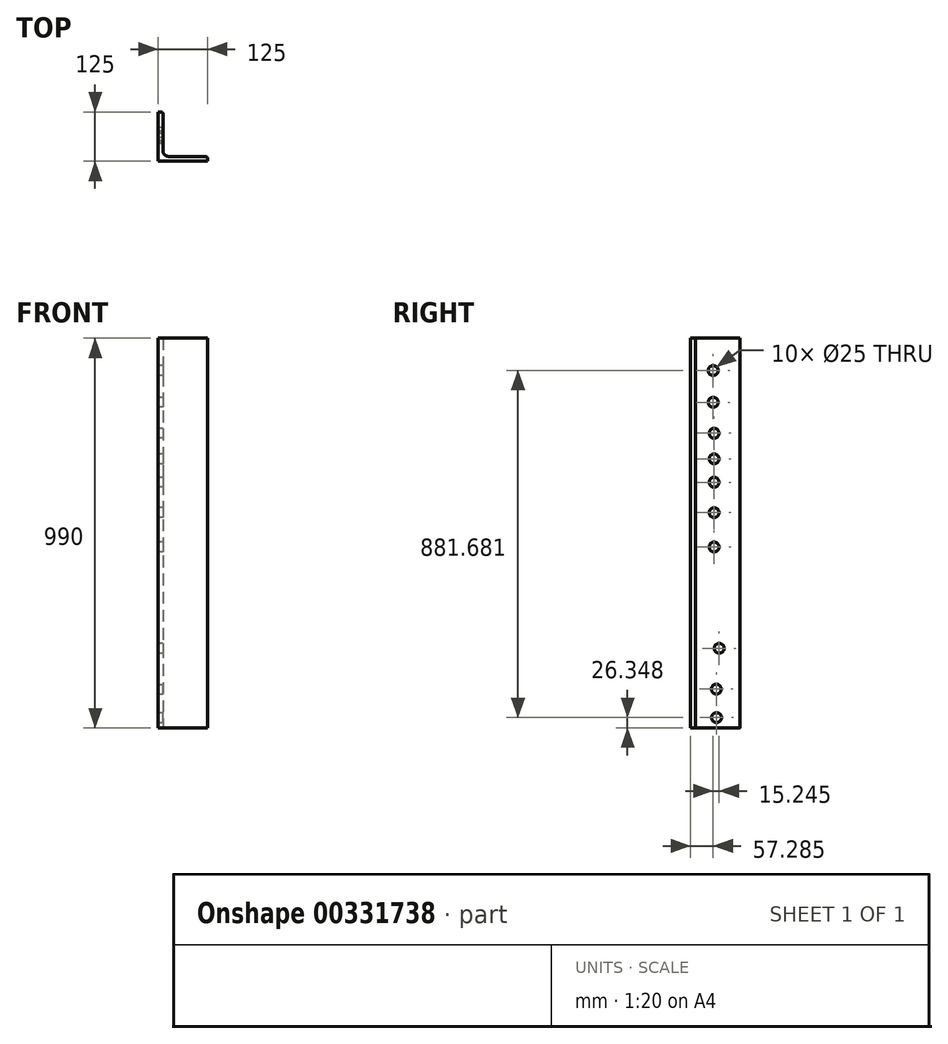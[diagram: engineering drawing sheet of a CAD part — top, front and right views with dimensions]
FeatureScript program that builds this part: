
annotation { "Feature Type Name" : "Feature", "Feature Type Description" : "" }
export const myFeature = defineFeature(function(context is Context, id is Id, definition is map)
    precondition{}
    {
        {
            var Q0;
            Q0=qCreatedBy(makeId("Top.planeOp"),FACE);
            var sketch = newSketch(context, id + "F0", { "sketchPlane" : qUnion([Q0])});
            skLineSegment(sketch, "E0", {"start": v(0, 0) * mm, "end": v(125, 0) * mm});
            skLineSegment(sketch, "E1", {"start": v(125, 0) * mm, "end": v(125, 12) * mm});
            skLineSegment(sketch, "E2", {"start": v(125, 12) * mm, "end": v(12, 12) * mm});
            skLineSegment(sketch, "E3", {"start": v(12, 12) * mm, "end": v(12, 125) * mm});
            skLineSegment(sketch, "E4", {"start": v(12, 125) * mm, "end": v(0, 125) * mm});
            skLineSegment(sketch, "E5", {"start": v(0, 125) * mm, "end": v(0, 0) * mm});
            skSolve(sketch);
        }
        {
            var Q0;
            Q0 = qSketchRegion(id + "F0", true);
            extrude(context, id + "F1", {"entities" : qUnion([Q0]), "depth" : 990 * mm});
        }
        {
            var Q0;
            Q0=makeQuery(id+"F1.opExtrude","SWEPT_EDGE",EDGE,{"disambiguationData":[OSD([sQuery(id+"F0.wireOp",EDGE,"E3"),sQuery(id+"F0.wireOp",EDGE,"E4")])]});
            var Q1;
            Q1=makeQuery(id+"F1.opExtrude","SWEPT_EDGE",EDGE,{"disambiguationData":[OSD([sQuery(id+"F0.wireOp",EDGE,"E1"),sQuery(id+"F0.wireOp",EDGE,"E2")])]});
            fillet(context, id + "F2", {"entities" : qUnion([Q0, Q1]), "radius" : 4.6 * mm, "tangentPropagation" : true, "allowEdgeOverflow" : false});
        }
        {
            var Q0;
            Q0=makeQuery(id+"F1.opExtrude","SWEPT_EDGE",EDGE,{"disambiguationData":[OSD([sQuery(id+"F0.wireOp",EDGE,"E2"),sQuery(id+"F0.wireOp",EDGE,"E3")])]});
            fillet(context, id + "F3", {"entities" : qUnion([Q0]), "radius" : 14 * mm, "tangentPropagation" : true, "allowEdgeOverflow" : false});
        }
        {
            var Q0;
            Q0=makeQuery(id+"F1.opExtrude","SWEPT_FACE",FACE,{"disambiguationData":[OSD([sQuery(id+"F0.wireOp",EDGE,"E5")])]});
            var sketch = newSketch(context, id + "F4", { "sketchPlane" : qUnion([Q0])});
            skPoint(sketch, "E6", {"position": v(-57.29, 827.31) * mm});
            skPoint(sketch, "E7", {"position": v(-57.29, 908.03) * mm});
            skPoint(sketch, "E8", {"position": v(-59.56, 748.72) * mm});
            skPoint(sketch, "E9", {"position": v(-59.56, 683.5) * mm});
            skPoint(sketch, "E10", {"position": v(-59.56, 624.14) * mm});
            skPoint(sketch, "E11", {"position": v(-59.56, 547.02) * mm});
            skPoint(sketch, "E12", {"position": v(-59.56, 459.62) * mm});
            skSolve(sketch);
        }
        {
            var Q0;
            Q0=sQuery(id+"F4.wireOp",VERTEX,"E7");
            var Q1;
            Q1=sQuery(id+"F4.wireOp",VERTEX,"E12");
            var Q2;
            Q2=sQuery(id+"F4.wireOp",VERTEX,"E11");
            var Q3;
            Q3=sQuery(id+"F4.wireOp",VERTEX,"E10");
            var Q4;
            Q4=sQuery(id+"F4.wireOp",VERTEX,"E9");
            var Q5;
            Q5=sQuery(id+"F4.wireOp",VERTEX,"E8");
            var Q6;
            Q6=sQuery(id+"F4.wireOp",VERTEX,"E6");
            var Q7;
            Q7=makeQuery(id+"F1.opExtrude","SWEPT_BODY",BODY,{"disambiguationData":[OSD([sQuery(id+"F0.wireOp",EDGE,"E0"),sQuery(id+"F0.wireOp",EDGE,"E1"),sQuery(id+"F0.wireOp",EDGE,"E2"),sQuery(id+"F0.wireOp",EDGE,"E3"),sQuery(id+"F0.wireOp",EDGE,"E4"),sQuery(id+"F0.wireOp",EDGE,"E5")])]});
            hole(context, id + "F5", {"style" : HoleStyle.SIMPLE, "endStyle" : HoleEndStyle.THROUGH, "holeDiameter" : 25 * mm, "tappedDepth" : 12 * mm, "tapClearance" : 3, "locations" : qUnion([Q0, Q1, Q2, Q3, Q4, Q5, Q6]), "scope" : qUnion([Q7])});
        }
        {
            var Q0;
            Q0=makeQuery(id+"F1.opExtrude","SWEPT_FACE",FACE,{"disambiguationData":[OSD([sQuery(id+"F0.wireOp",EDGE,"E5")])]});
            var sketch = newSketch(context, id + "F6", { "sketchPlane" : qUnion([Q0])});
            skPoint(sketch, "E13", {"position": v(-72.53, 202.23) * mm});
            skArc(sketch, "E14", {"start": v(-85.03, 202.23) * mm, "mid": v(-72.53, 214.73) * mm, "end": v(-60.03, 202.23) * mm});
            skArc(sketch, "E15", {"start": v(-85.03, 202.23) * mm, "mid": v(-72.53, 189.73) * mm, "end": v(-60.03, 202.23) * mm});
            skSolve(sketch);
        }
        {
            var Q0;
            Q0=sQuery(id+"F6.wireOp",VERTEX,"E13");
            var Q1;
            Q1=makeQuery(id+"F1.opExtrude","SWEPT_BODY",BODY,{"disambiguationData":[OSD([sQuery(id+"F0.wireOp",EDGE,"E0"),sQuery(id+"F0.wireOp",EDGE,"E1"),sQuery(id+"F0.wireOp",EDGE,"E2"),sQuery(id+"F0.wireOp",EDGE,"E3"),sQuery(id+"F0.wireOp",EDGE,"E4"),sQuery(id+"F0.wireOp",EDGE,"E5")])]});
            hole(context, id + "F7", {"style" : HoleStyle.SIMPLE, "endStyle" : HoleEndStyle.THROUGH, "holeDiameter" : 25 * mm, "tappedDepth" : 12 * mm, "tapClearance" : 3, "locations" : qUnion([Q0]), "scope" : qUnion([Q1])});
        }
        {
            var Q0;
            Q0=makeQuery(id+"F1.opExtrude","SWEPT_FACE",FACE,{"disambiguationData":[OSD([sQuery(id+"F0.wireOp",EDGE,"E3")])]});
            var sketch = newSketch(context, id + "F8", { "sketchPlane" : qUnion([Q0])});
            skPoint(sketch, "E16", {"position": v(65.76, 26.35) * mm});
            skSolve(sketch);
        }
        {
            var Q0;
            Q0=sQuery(id+"F8.wireOp",VERTEX,"E16");
            var Q1;
            Q1=makeQuery(id+"F1.opExtrude","SWEPT_BODY",BODY,{"disambiguationData":[OSD([sQuery(id+"F0.wireOp",EDGE,"E0"),sQuery(id+"F0.wireOp",EDGE,"E1"),sQuery(id+"F0.wireOp",EDGE,"E2"),sQuery(id+"F0.wireOp",EDGE,"E3"),sQuery(id+"F0.wireOp",EDGE,"E4"),sQuery(id+"F0.wireOp",EDGE,"E5")])]});
            hole(context, id + "F9", {"style" : HoleStyle.SIMPLE, "endStyle" : HoleEndStyle.THROUGH, "holeDiameter" : 25 * mm, "tappedDepth" : 12 * mm, "tapClearance" : 3, "locations" : qUnion([Q0]), "scope" : qUnion([Q1])});
        }
        {
            var Q0;
            Q0=makeQuery(id+"F1.opExtrude","SWEPT_FACE",FACE,{"disambiguationData":[OSD([sQuery(id+"F0.wireOp",EDGE,"E3")])]});
            var sketch = newSketch(context, id + "F10", { "sketchPlane" : qUnion([Q0])});
            skPoint(sketch, "E17", {"position": v(65.28, 98.54) * mm});
            skSolve(sketch);
        }
        {
            var Q0;
            Q0=sQuery(id+"F10.wireOp",VERTEX,"E17");
            var Q1;
            Q1=makeQuery(id+"F1.opExtrude","SWEPT_BODY",BODY,{"disambiguationData":[OSD([sQuery(id+"F0.wireOp",EDGE,"E0"),sQuery(id+"F0.wireOp",EDGE,"E1"),sQuery(id+"F0.wireOp",EDGE,"E2"),sQuery(id+"F0.wireOp",EDGE,"E3"),sQuery(id+"F0.wireOp",EDGE,"E4"),sQuery(id+"F0.wireOp",EDGE,"E5")])]});
            hole(context, id + "F11", {"style" : HoleStyle.SIMPLE, "endStyle" : HoleEndStyle.THROUGH, "holeDiameter" : 25 * mm, "tappedDepth" : 12 * mm, "tapClearance" : 3, "locations" : qUnion([Q0]), "scope" : qUnion([Q1])});
        }
    });
